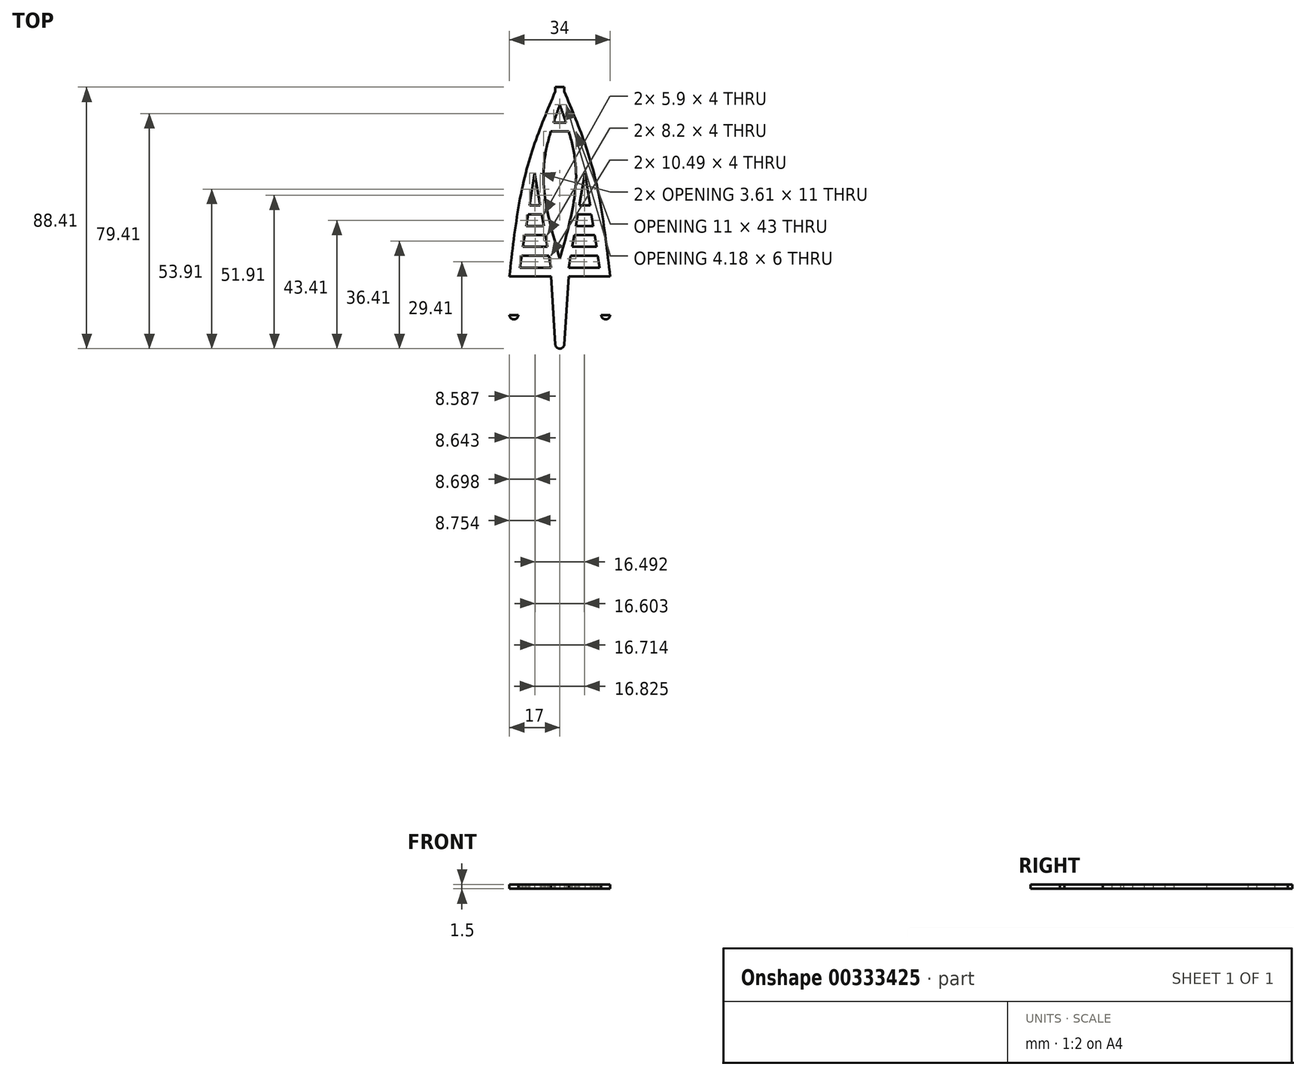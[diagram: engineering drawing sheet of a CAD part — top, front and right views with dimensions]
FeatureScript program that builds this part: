
annotation { "Feature Type Name" : "Feature", "Feature Type Description" : "" }
export const myFeature = defineFeature(function(context is Context, id is Id, definition is map)
    precondition{}
    {
        {
            var Q0;
            Q0=qCreatedBy(makeId("Top.planeOp"),FACE);
            var sketch = newSketch(context, id + "F0", { "sketchPlane" : qUnion([Q0])});
            skLineSegment(sketch, "E0", {"start": v(-1.5, 0) * mm, "end": v(1.5, 0) * mm});
            skArc(sketch, "E1", {"start": v(-1.5, 0) * mm, "mid": v(0, 1.5) * mm, "end": v(1.5, 0) * mm});
            skLineSegment(sketch, "E2.top", {"start": v(-1.5, -1.5) * mm, "end": v(1.5, -1.5) * mm});
            skLineSegment(sketch, "E2.left", {"start": v(-1.5, 0) * mm, "end": v(-1.5, -1.5) * mm});
            skLineSegment(sketch, "E2.right", {"start": v(1.5, 0) * mm, "end": v(1.5, -1.5) * mm});
            skLineSegment(sketch, "E3", {"start": v(0, 0) * mm, "end": v(0, -15) * mm});
            skPoint(sketch, "E4", {"position": v(0, -12) * mm});
            skPoint(sketch, "E5", {"position": v(0, -6) * mm});
            skLineSegment(sketch, "E6", {"start": v(0, -15) * mm, "end": v(0, -64) * mm});
            skPoint(sketch, "E7", {"position": v(0, -29) * mm});
            skLineSegment(sketch, "E8", {"start": v(-5.5, -29) * mm, "end": v(5.5, -29) * mm});
            skLineSegment(sketch, "E9", {"start": v(0, -6) * mm, "end": v(-5.5, -29) * mm});
            skLineSegment(sketch, "E10", {"start": v(0, -6) * mm, "end": v(5.5, -29) * mm});
            skPoint(sketch, "E11", {"position": v(0, -58) * mm});
            skLineSegment(sketch, "E12", {"start": v(0, -58) * mm, "end": v(-5.5, -29) * mm});
            skLineSegment(sketch, "E13", {"start": v(0, -58) * mm, "end": v(5.5, -29) * mm});
            skLineSegment(sketch, "E14", {"start": v(-5.5, -29) * mm, "end": v(-11.5, -29) * mm});
            skLineSegment(sketch, "E15", {"start": v(5.5, -29) * mm, "end": v(11.5, -29) * mm});
            skLineSegment(sketch, "E16", {"start": v(-11.5, -29) * mm, "end": v(-1.5, -1.5) * mm});
            skLineSegment(sketch, "E17", {"start": v(11.5, -29) * mm, "end": v(1.5, -1.5) * mm});
            skLineSegment(sketch, "E18", {"start": v(-17, -64) * mm, "end": v(17, -64) * mm});
            skLineSegment(sketch, "E19", {"start": v(-17, -64) * mm, "end": v(-11.5, -29) * mm});
            skLineSegment(sketch, "E20", {"start": v(17, -64) * mm, "end": v(11.5, -29) * mm});
            skPoint(sketch, "E21", {"position": v(-8.5, -29) * mm});
            skPoint(sketch, "E22", {"position": v(8.5, -29) * mm});
            skPoint(sketch, "E23", {"position": v(-13.5, -61) * mm});
            skPoint(sketch, "E24", {"position": v(-3, -61) * mm});
            skLineSegment(sketch, "E25", {"start": v(-3, -61) * mm, "end": v(-13.5, -61) * mm});
            skLineSegment(sketch, "E26", {"start": v(-13.5, -61) * mm, "end": v(-8.5, -29) * mm});
            skLineSegment(sketch, "E27", {"start": v(-8.5, -29) * mm, "end": v(-3, -61) * mm});
            skPoint(sketch, "E28", {"position": v(13.5, -61) * mm});
            skPoint(sketch, "E29", {"position": v(3, -61) * mm});
            skLineSegment(sketch, "E30", {"start": v(3, -61) * mm, "end": v(13.5, -61) * mm});
            skLineSegment(sketch, "E31", {"start": v(13.5, -61) * mm, "end": v(8.5, -29) * mm});
            skLineSegment(sketch, "E32", {"start": v(8.5, -29) * mm, "end": v(3, -61) * mm});
            skLineSegment(sketch, "E33", {"start": v(-3, -64) * mm, "end": v(3, -64) * mm});
            skLineSegment(sketch, "E34", {"start": v(0, -64) * mm, "end": v(0, -87) * mm});
            skLineSegment(sketch, "E35", {"start": v(-1.5, -87) * mm, "end": v(1.5, -87) * mm});
            skLineSegment(sketch, "E36", {"start": v(-1.5, -87) * mm, "end": v(-3, -64) * mm});
            skLineSegment(sketch, "E37", {"start": v(3, -64) * mm, "end": v(1.5, -87) * mm});
            skPoint(sketch, "E38", {"position": v(14, -64) * mm});
            skPoint(sketch, "E39", {"position": v(-14, -64) * mm});
            skLineSegment(sketch, "E40.bottom", {"start": v(-17, -64) * mm, "end": v(-14, -64) * mm});
            skLineSegment(sketch, "E40.top", {"start": v(-17, -77) * mm, "end": v(-14, -77) * mm});
            skLineSegment(sketch, "E40.left", {"start": v(-17, -64) * mm, "end": v(-17, -77) * mm});
            skLineSegment(sketch, "E40.right", {"start": v(-14, -64) * mm, "end": v(-14, -77) * mm});
            skLineSegment(sketch, "E41.bottom", {"start": v(17, -64) * mm, "end": v(14, -64) * mm});
            skLineSegment(sketch, "E41.top", {"start": v(17, -77) * mm, "end": v(14, -77) * mm});
            skLineSegment(sketch, "E41.left", {"start": v(17, -64) * mm, "end": v(17, -77) * mm});
            skLineSegment(sketch, "E41.right", {"start": v(14, -64) * mm, "end": v(14, -77) * mm});
            skArc(sketch, "E42", {"start": v(-17, -77) * mm, "mid": v(-15.5, -78.5) * mm, "end": v(-14, -77) * mm});
            skArc(sketch, "E43", {"start": v(14, -77) * mm, "mid": v(15.5, -78.5) * mm, "end": v(17, -77) * mm});
            skArc(sketch, "E44", {"start": v(-1.5, -87) * mm, "mid": v(0, -88.4) * mm, "end": v(1.5, -87) * mm});
            skLineSegment(sketch, "E45", {"start": v(-8.5, -29) * mm, "end": v(-8.5, -61) * mm});
            skLineSegment(sketch, "E46", {"start": v(-12.87, -57) * mm, "end": v(-3.69, -57) * mm});
            skLineSegment(sketch, "E47", {"start": v(-12.4, -54) * mm, "end": v(-4.2, -54) * mm});
            skLineSegment(sketch, "E48", {"start": v(-11.78, -50) * mm, "end": v(-4.9, -50) * mm});
            skLineSegment(sketch, "E49", {"start": v(-11.3, -47) * mm, "end": v(-5.4, -47) * mm});
            skLineSegment(sketch, "E50", {"start": v(-10.68, -43) * mm, "end": v(-6.1, -43) * mm});
            skLineSegment(sketch, "E51", {"start": v(-10.22, -40) * mm, "end": v(-6.6, -40) * mm});
            skLineSegment(sketch, "E52", {"start": v(3.69, -57) * mm, "end": v(12.87, -57) * mm});
            skLineSegment(sketch, "E53", {"start": v(4.2, -54) * mm, "end": v(12.4, -54) * mm});
            skLineSegment(sketch, "E54", {"start": v(4.9, -50) * mm, "end": v(11.78, -50) * mm});
            skLineSegment(sketch, "E55", {"start": v(5.4, -47) * mm, "end": v(11.3, -47) * mm});
            skLineSegment(sketch, "E56", {"start": v(6.1, -43) * mm, "end": v(10.68, -43) * mm});
            skLineSegment(sketch, "E57", {"start": v(6.6, -40) * mm, "end": v(10.22, -40) * mm});
            skFitSpline(sketch, "E58", {"points": [v(0, -58) * mm, v(-5.5, -29) * mm, v(0, -6) * mm], "startDerivative": vector(-16.25, 56.6) * mm, "endDerivative": vector(16.86, 47.22) * mm});
            skFitSpline(sketch, "E59", {"points": [v(0, -58) * mm, v(5.5, -29) * mm, v(0, -6) * mm], "startDerivative": vector(16.25, 56.6) * mm, "endDerivative": vector(-16.86, 47.22) * mm});
            skFitSpline(sketch, "E60", {"points": [v(-17, -64) * mm, v(-11.5, -29) * mm, v(-1.5, -1.5) * mm], "startDerivative": vector(7.75, 69.18) * mm, "endDerivative": vector(23.5, 55.6) * mm});
            skFitSpline(sketch, "E61", {"points": [v(17, -64) * mm, v(11.5, -29) * mm, v(1.5, -1.5) * mm], "startDerivative": vector(-7.75, 69.18) * mm, "endDerivative": vector(-23.5, 55.6) * mm});
            skLineSegment(sketch, "E62", {"start": v(-2.09, -12) * mm, "end": v(2.09, -12) * mm});
            skLineSegment(sketch, "E63", {"start": v(-3.04, -15) * mm, "end": v(3.04, -15) * mm});
            skSolve(sketch);
        }
        {
            var Q0;
            {var subQ0=sQuery(id+"F0.wireOp",EDGE,"E1");Q0=makeQuery(id+"F0.imprint","IMPRINT",FACE,{"disambiguationData":[TD([[makeQuery(id+"F0.imprint","IMPRINT",EDGE,{"derivedFrom":subQ0}),-1.0]])]});}
            var Q1;
            {var subQ0=sQuery(id+"F0.wireOp",EDGE,"E2.left");Q1=makeQuery(id+"F0.imprint","IMPRINT",FACE,{"disambiguationData":[TD([[makeQuery(id+"F0.imprint","IMPRINT",EDGE,{"derivedFrom":subQ0}),1.0]])]});}
            var Q2;
            {var subQ0=sQuery(id+"F0.wireOp",EDGE,"E2.right");Q2=makeQuery(id+"F0.imprint","IMPRINT",FACE,{"disambiguationData":[TD([[makeQuery(id+"F0.imprint","IMPRINT",EDGE,{"derivedFrom":subQ0}),-1.0]])]});}
            var Q3;
            {var subQ0=sQuery(id+"F0.wireOp",EDGE,"E16");Q3=makeQuery(id+"F0.imprint","IMPRINT",FACE,{"disambiguationData":[TD([[makeQuery(id+"F0.imprint","IMPRINT",EDGE,{"derivedFrom":subQ0}),1.0]])]});}
            var Q4;
            {var subQ1=sQuery(id+"F0.wireOp",EDGE,"E16");Q4=makeQuery(id+"F0.imprint","IMPRINT",FACE,{"disambiguationData":[TD([[makeQuery(id+"F0.imprint","IMPRINT",EDGE,{"derivedFrom":subQ1}),-1.0]])]});}
            var Q5;
            {var subQ0=sQuery(id+"F0.wireOp",EDGE,"E62");var subQ1=sQuery(id+"F0.wireOp",EDGE,"E9");var subQ2=makeQuery(id+"F0.imprint","INTERSECT",VERTEX,{"derivedFrom":[subQ1,subQ0]});Q5=makeQuery(id+"F0.imprint","IMPRINT",FACE,{"disambiguationData":[TD([[makeQuery(id+"F0.imprint","IMPRINT",EDGE,{"disambiguationData":[TD([[subQ2,-1.0]])],"derivedFrom":subQ1}),-1.0]])]});}
            var Q6;
            {var subQ3=sQuery(id+"F0.wireOp",EDGE,"E62");var subQ5=sQuery(id+"F0.wireOp",EDGE,"E9");var subQ7=makeQuery(id+"F0.imprint","INTERSECT",VERTEX,{"derivedFrom":[subQ5,subQ3]});Q6=makeQuery(id+"F0.imprint","IMPRINT",FACE,{"disambiguationData":[TD([[makeQuery(id+"F0.imprint","IMPRINT",EDGE,{"disambiguationData":[TD([[subQ7,-1.0]])],"derivedFrom":subQ5}),1.0]])]});}
            var Q7;
            {var subQ3=sQuery(id+"F0.wireOp",EDGE,"E62");var subQ5=sQuery(id+"F0.wireOp",EDGE,"E10");var subQ6=makeQuery(id+"F0.imprint","INTERSECT",VERTEX,{"derivedFrom":[subQ5,subQ3]});Q7=makeQuery(id+"F0.imprint","IMPRINT",FACE,{"disambiguationData":[TD([[makeQuery(id+"F0.imprint","IMPRINT",EDGE,{"disambiguationData":[TD([[subQ6,-1.0]])],"derivedFrom":subQ5}),-1.0]])]});}
            var Q8;
            {var subQ0=sQuery(id+"F0.wireOp",EDGE,"E62");var subQ1=sQuery(id+"F0.wireOp",EDGE,"E10");var subQ2=makeQuery(id+"F0.imprint","INTERSECT",VERTEX,{"derivedFrom":[subQ1,subQ0]});Q8=makeQuery(id+"F0.imprint","IMPRINT",FACE,{"disambiguationData":[TD([[makeQuery(id+"F0.imprint","IMPRINT",EDGE,{"disambiguationData":[TD([[subQ2,-1.0]])],"derivedFrom":subQ1}),1.0]])]});}
            var Q9;
            {var subQ0=sQuery(id+"F0.wireOp",EDGE,"E17");Q9=makeQuery(id+"F0.imprint","IMPRINT",FACE,{"disambiguationData":[TD([[makeQuery(id+"F0.imprint","IMPRINT",EDGE,{"derivedFrom":subQ0}),-1.0]])]});}
            var Q10;
            {var subQ1=sQuery(id+"F0.wireOp",EDGE,"E17");Q10=makeQuery(id+"F0.imprint","IMPRINT",FACE,{"disambiguationData":[TD([[makeQuery(id+"F0.imprint","IMPRINT",EDGE,{"derivedFrom":subQ1}),1.0]])]});}
            var Q11;
            {var subQ29=sQuery(id+"F0.wireOp",EDGE,"E19");Q11=makeQuery(id+"F0.imprint","IMPRINT",FACE,{"disambiguationData":[TD([[makeQuery(id+"F0.imprint","IMPRINT",EDGE,{"derivedFrom":subQ29}),-1.0]])]});}
            var Q12;
            {var subQ0=sQuery(id+"F0.wireOp",EDGE,"E19");Q12=makeQuery(id+"F0.imprint","IMPRINT",FACE,{"disambiguationData":[TD([[makeQuery(id+"F0.imprint","IMPRINT",EDGE,{"derivedFrom":subQ0}),1.0]])]});}
            var Q13;
            {var subQ32=sQuery(id+"F0.wireOp",EDGE,"E20");Q13=makeQuery(id+"F0.imprint","IMPRINT",FACE,{"disambiguationData":[TD([[makeQuery(id+"F0.imprint","IMPRINT",EDGE,{"derivedFrom":subQ32}),1.0]])]});}
            var Q14;
            {var subQ0=sQuery(id+"F0.wireOp",EDGE,"E20");Q14=makeQuery(id+"F0.imprint","IMPRINT",FACE,{"disambiguationData":[TD([[makeQuery(id+"F0.imprint","IMPRINT",EDGE,{"derivedFrom":subQ0}),-1.0]])]});}
            var Q15;
            {var subQ0=sQuery(id+"F0.wireOp",EDGE,"E56");Q15=makeQuery(id+"F0.imprint","IMPRINT",FACE,{"disambiguationData":[TD([[makeQuery(id+"F0.imprint","IMPRINT",EDGE,{"derivedFrom":subQ0}),1.0]])]});}
            var Q16;
            {var subQ0=sQuery(id+"F0.wireOp",EDGE,"E54");Q16=makeQuery(id+"F0.imprint","IMPRINT",FACE,{"disambiguationData":[TD([[makeQuery(id+"F0.imprint","IMPRINT",EDGE,{"derivedFrom":subQ0}),1.0]])]});}
            var Q17;
            {var subQ0=sQuery(id+"F0.wireOp",EDGE,"E52");Q17=makeQuery(id+"F0.imprint","IMPRINT",FACE,{"disambiguationData":[TD([[makeQuery(id+"F0.imprint","IMPRINT",EDGE,{"derivedFrom":subQ0}),1.0]])]});}
            var Q18;
            {var subQ0=sQuery(id+"F0.wireOp",EDGE,"E46");var subQ1=sQuery(id+"F0.wireOp",EDGE,"E26");var subQ2=makeQuery(id+"F0.imprint","INTERSECT",VERTEX,{"derivedFrom":[subQ1,subQ0]});Q18=makeQuery(id+"F0.imprint","IMPRINT",FACE,{"disambiguationData":[TD([[makeQuery(id+"F0.imprint","IMPRINT",EDGE,{"disambiguationData":[TD([[subQ2,-1.0]])],"derivedFrom":subQ1}),-1.0]])]});}
            var Q19;
            {var subQ0=sQuery(id+"F0.wireOp",EDGE,"E46");var subQ1=sQuery(id+"F0.wireOp",EDGE,"E27");var subQ2=makeQuery(id+"F0.imprint","INTERSECT",VERTEX,{"derivedFrom":[subQ1,subQ0]});Q19=makeQuery(id+"F0.imprint","IMPRINT",FACE,{"disambiguationData":[TD([[makeQuery(id+"F0.imprint","IMPRINT",EDGE,{"disambiguationData":[TD([[subQ2,1.0]])],"derivedFrom":subQ1}),-1.0]])]});}
            var Q20;
            {var subQ0=sQuery(id+"F0.wireOp",EDGE,"E48");var subQ1=sQuery(id+"F0.wireOp",EDGE,"E27");var subQ2=makeQuery(id+"F0.imprint","INTERSECT",VERTEX,{"derivedFrom":[subQ1,subQ0]});Q20=makeQuery(id+"F0.imprint","IMPRINT",FACE,{"disambiguationData":[TD([[makeQuery(id+"F0.imprint","IMPRINT",EDGE,{"disambiguationData":[TD([[subQ2,1.0]])],"derivedFrom":subQ1}),-1.0]])]});}
            var Q21;
            {var subQ0=sQuery(id+"F0.wireOp",EDGE,"E48");var subQ1=sQuery(id+"F0.wireOp",EDGE,"E26");var subQ2=makeQuery(id+"F0.imprint","INTERSECT",VERTEX,{"derivedFrom":[subQ1,subQ0]});Q21=makeQuery(id+"F0.imprint","IMPRINT",FACE,{"disambiguationData":[TD([[makeQuery(id+"F0.imprint","IMPRINT",EDGE,{"disambiguationData":[TD([[subQ2,-1.0]])],"derivedFrom":subQ1}),-1.0]])]});}
            var Q22;
            {var subQ0=sQuery(id+"F0.wireOp",EDGE,"E50");var subQ1=sQuery(id+"F0.wireOp",EDGE,"E26");var subQ2=makeQuery(id+"F0.imprint","INTERSECT",VERTEX,{"derivedFrom":[subQ1,subQ0]});Q22=makeQuery(id+"F0.imprint","IMPRINT",FACE,{"disambiguationData":[TD([[makeQuery(id+"F0.imprint","IMPRINT",EDGE,{"disambiguationData":[TD([[subQ2,-1.0]])],"derivedFrom":subQ1}),-1.0]])]});}
            var Q23;
            {var subQ0=sQuery(id+"F0.wireOp",EDGE,"E50");var subQ1=sQuery(id+"F0.wireOp",EDGE,"E27");var subQ2=makeQuery(id+"F0.imprint","INTERSECT",VERTEX,{"derivedFrom":[subQ1,subQ0]});Q23=makeQuery(id+"F0.imprint","IMPRINT",FACE,{"disambiguationData":[TD([[makeQuery(id+"F0.imprint","IMPRINT",EDGE,{"disambiguationData":[TD([[subQ2,1.0]])],"derivedFrom":subQ1}),-1.0]])]});}
            var Q24;
            Q24=makeQuery(id+"F0.imprint","IMPRINT",FACE,{"disambiguationData":[TD([[makeQuery(id+"F0.imprint","IMPRINT",EDGE,{"derivedFrom":sQuery(id+"F0.wireOp",EDGE,"E40.bottom")}),-1.0]])]});
            var Q25;
            {var subQ0=sQuery(id+"F0.wireOp",EDGE,"E34");Q25=makeQuery(id+"F0.imprint","IMPRINT",FACE,{"disambiguationData":[TD([[makeQuery(id+"F0.imprint","IMPRINT",EDGE,{"derivedFrom":subQ0}),-1.0]])]});}
            var Q26;
            Q26=makeQuery(id+"F0.imprint","IMPRINT",FACE,{"disambiguationData":[TD([[makeQuery(id+"F0.imprint","IMPRINT",EDGE,{"derivedFrom":sQuery(id+"F0.wireOp",EDGE,"E41.bottom")}),1.0]])]});
            var Q27;
            {var subQ0=sQuery(id+"F0.wireOp",EDGE,"E34");Q27=makeQuery(id+"F0.imprint","IMPRINT",FACE,{"disambiguationData":[TD([[makeQuery(id+"F0.imprint","IMPRINT",EDGE,{"derivedFrom":subQ0}),1.0]])]});}
            var Q28;
            Q28=makeQuery(id+"F0.imprint","IMPRINT",FACE,{"disambiguationData":[TD([[makeQuery(id+"F0.imprint","IMPRINT",EDGE,{"derivedFrom":sQuery(id+"F0.wireOp",EDGE,"E41.top")}),1.0]])]});
            var Q29;
            Q29=makeQuery(id+"F0.imprint","IMPRINT",FACE,{"disambiguationData":[TD([[makeQuery(id+"F0.imprint","IMPRINT",EDGE,{"derivedFrom":sQuery(id+"F0.wireOp",EDGE,"E40.top")}),-1.0]])]});
            var Q30;
            {var subQ2=sQuery(id+"F0.wireOp",EDGE,"E44");Q30=makeQuery(id+"F0.imprint","IMPRINT",FACE,{"disambiguationData":[TD([[makeQuery(id+"F0.imprint","IMPRINT",EDGE,{"derivedFrom":subQ2}),1.0]])]});}
            extrude(context, id + "F1", {"entities" : qUnion([Q0, Q1, Q2, Q3, Q4, Q5, Q6, Q7, Q8, Q9, Q10, Q11, Q12, Q13, Q14, Q15, Q16, Q17, Q18, Q19, Q20, Q21, Q22, Q23, Q24, Q25, Q26, Q27, Q28, Q29, Q30]), "depth" : 1.5 * mm});
        }
    });
